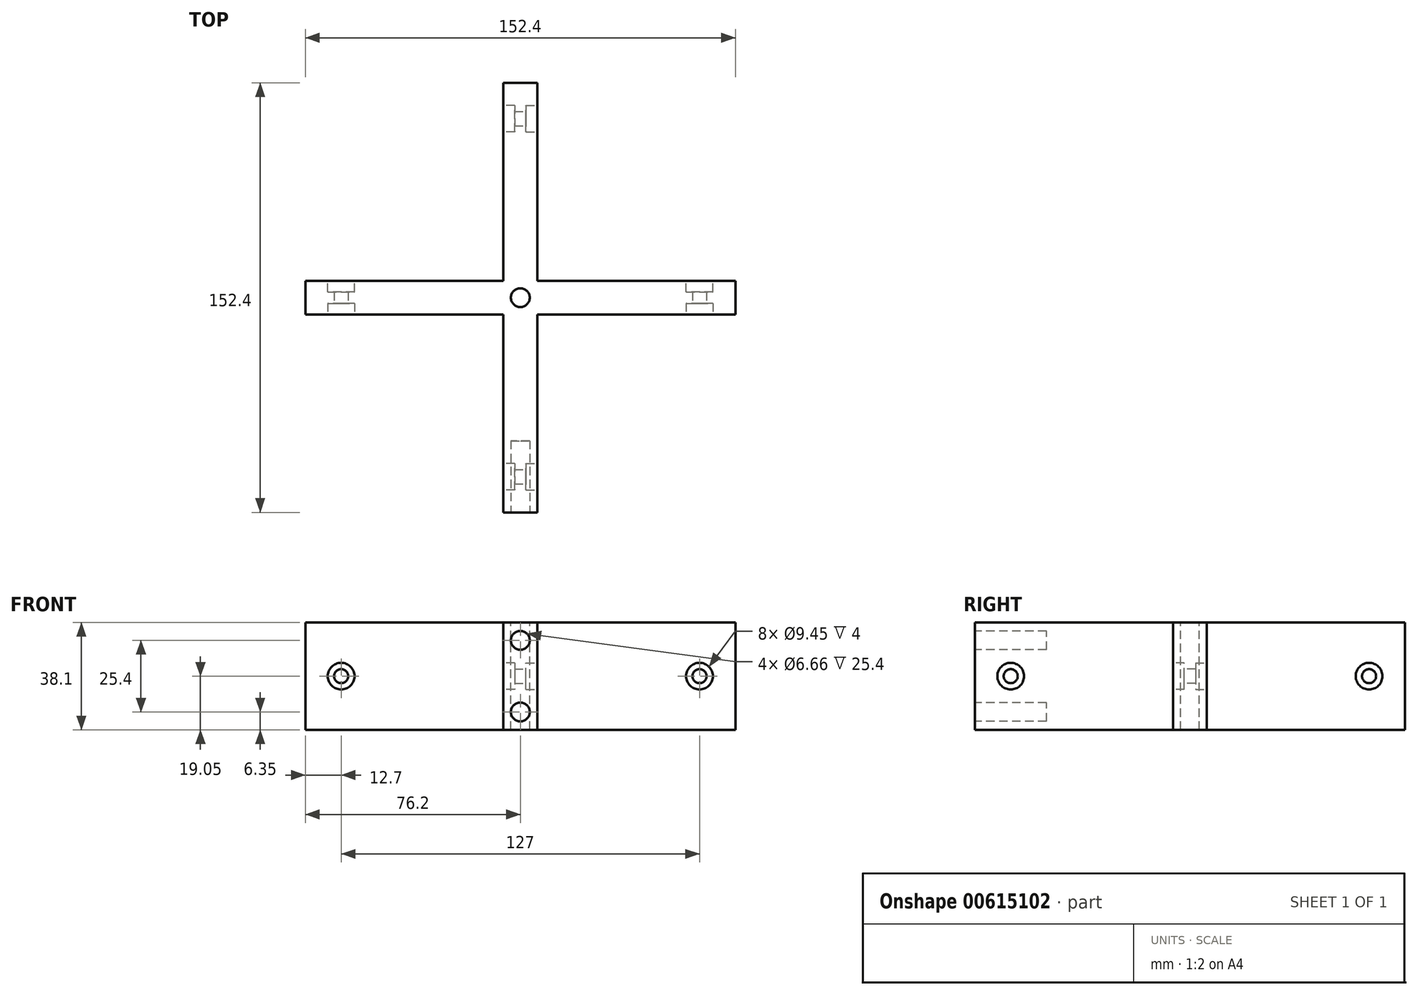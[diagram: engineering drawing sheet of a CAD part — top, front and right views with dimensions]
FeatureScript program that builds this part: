
annotation { "Feature Type Name" : "Feature", "Feature Type Description" : "" }
export const myFeature = defineFeature(function(context is Context, id is Id, definition is map)
    precondition{}
    {
        {
            var Q0;
            Q0=qCreatedBy(makeId("Top.planeOp"),FACE);
            var sketch = newSketch(context, id + "F0", { "sketchPlane" : qUnion([Q0])});
            skLineSegment(sketch, "E0.bottom", {"start": v(-6, 76.2) * mm, "end": v(6, 76.2) * mm});
            skLineSegment(sketch, "E0.top", {"start": v(-6, -76.2) * mm, "end": v(6, -76.2) * mm});
            skLineSegment(sketch, "E0.left", {"start": v(-6, 76.2) * mm, "end": v(-6, -76.2) * mm});
            skLineSegment(sketch, "E0.right", {"start": v(6, 76.2) * mm, "end": v(6, -76.2) * mm});
            skPoint(sketch, "E0.middle", {"position": v(0, 0) * mm});
            skLineSegment(sketch, "E1.bottom", {"start": v(-76.2, 6) * mm, "end": v(76.2, 6) * mm});
            skLineSegment(sketch, "E1.top", {"start": v(-76.2, -6) * mm, "end": v(76.2, -6) * mm});
            skLineSegment(sketch, "E1.left", {"start": v(-76.2, 6) * mm, "end": v(-76.2, -6) * mm});
            skLineSegment(sketch, "E1.right", {"start": v(76.2, 6) * mm, "end": v(76.2, -6) * mm});
            skSolve(sketch);
        }
        {
            var Q0;
            Q0 = qSketchRegion(id + "F0", true);
            extrude(context, id + "F1", {"entities" : qUnion([Q0]), "endBound" : BoundingType.SYMMETRIC, "depth" : 38.1 * mm, "offsetDistance" : 25.4 * mm});
        }
        {
            var Q0;
            {var subQ0=sQuery(id+"F0.wireOp",EDGE,"E0.right");Q0=makeQuery(id+"F1.opExtrude","SWEPT_FACE",FACE,{"disambiguationData":[OSD([subQ0]),TDD([makeQuery(id+"F0.imprint","IMPRINT",EDGE,{"disambiguationData":[TD([[makeQuery(id+"F0.imprint","INTERSECT",VERTEX,{"derivedFrom":[sQuery(id+"F0.wireOp",EDGE,"E0.top"),subQ0]}),1.0]])],"derivedFrom":subQ0})])]});}
            var sketch = newSketch(context, id + "F2", { "sketchPlane" : qUnion([Q0])});
            skLineSegment(sketch, "E2.0.0", {"start": v(6, -19.05) * mm, "end": v(76.2, -19.05) * mm});
            skLineSegment(sketch, "E2.0.1", {"start": v(76.2, -19.05) * mm, "end": v(76.2, 19.05) * mm});
            skLineSegment(sketch, "E2.0.2", {"start": v(76.2, 19.05) * mm, "end": v(6, 19.05) * mm});
            skLineSegment(sketch, "E2.0.3", {"start": v(6, 19.05) * mm, "end": v(6, -19.05) * mm});
            skLineSegment(sketch, "E3.0.0", {"start": v(-76.2, -19.05) * mm, "end": v(-6, -19.05) * mm});
            skLineSegment(sketch, "E3.0.1", {"start": v(-6, -19.05) * mm, "end": v(-6, 19.05) * mm});
            skLineSegment(sketch, "E3.0.2", {"start": v(-6, 19.05) * mm, "end": v(-76.2, 19.05) * mm});
            skLineSegment(sketch, "E3.0.3", {"start": v(-76.2, 19.05) * mm, "end": v(-76.2, -19.05) * mm});
            skCircle(sketch, "E4", {"center": v(-63.5, 0) * mm, "radius": 4.72 * mm});
            skCircle(sketch, "E5", {"center": v(63.5, 0) * mm, "radius": 4.72 * mm});
            skSolve(sketch);
        }
        {
            var Q0;
            Q0=makeQuery(id+"F2.imprint","IMPRINT",FACE,{"disambiguationData":[TD([[makeQuery(id+"F2.imprint","IMPRINT",EDGE,{"derivedFrom":sQuery(id+"F2.wireOp",EDGE,"E4")}),1.0]])]});
            var Q1;
            Q1=makeQuery(id+"F2.imprint","IMPRINT",FACE,{"disambiguationData":[TD([[makeQuery(id+"F2.imprint","IMPRINT",EDGE,{"derivedFrom":sQuery(id+"F2.wireOp",EDGE,"E5")}),1.0]])]});
            extrude(context, id + "F3", {"entities" : qUnion([Q0, Q1]), "operationType" : NewBodyOperationType.REMOVE, "oppositeDirection" : true, "depth" : 4 * mm, "offsetDistance" : 25.4 * mm});
        }
        {
            var Q0;
            {var subQ0=sQuery(id+"F0.wireOp",EDGE,"E0.right");Q0=makeQuery(id+"F1.opExtrude","SWEPT_FACE",FACE,{"disambiguationData":[OSD([subQ0]),TDD([makeQuery(id+"F0.imprint","IMPRINT",EDGE,{"disambiguationData":[TD([[makeQuery(id+"F0.imprint","INTERSECT",VERTEX,{"derivedFrom":[sQuery(id+"F0.wireOp",EDGE,"E0.top"),subQ0]}),1.0]])],"derivedFrom":subQ0})])]});}
            var sketch = newSketch(context, id + "F4", { "sketchPlane" : qUnion([Q0])});
            skCircle(sketch, "E6.0", {"center": v(-63.5, 0) * mm, "radius": 4.72 * mm});
            skCircle(sketch, "E7.0", {"center": v(63.5, 0) * mm, "radius": 4.72 * mm});
            skCircle(sketch, "E8", {"center": v(-63.5, 0) * mm, "radius": 2.5 * mm});
            skCircle(sketch, "E9", {"center": v(63.5, 0) * mm, "radius": 2.5 * mm});
            skSolve(sketch);
        }
        {
            var Q0;
            Q0=makeQuery(id+"F4.imprint","IMPRINT",FACE,{"disambiguationData":[TD([[makeQuery(id+"F4.imprint","IMPRINT",EDGE,{"derivedFrom":sQuery(id+"F4.wireOp",EDGE,"E8")}),1.0]])]});
            var Q1;
            Q1=makeQuery(id+"F4.imprint","IMPRINT",FACE,{"disambiguationData":[TD([[makeQuery(id+"F4.imprint","IMPRINT",EDGE,{"derivedFrom":sQuery(id+"F4.wireOp",EDGE,"E9")}),1.0]])]});
            extrude(context, id + "F5", {"entities" : qUnion([Q0, Q1]), "operationType" : NewBodyOperationType.REMOVE, "endBound" : BoundingType.THROUGH_ALL, "oppositeDirection" : true, "depth" : 6 * mm, "offsetDistance" : 25.4 * mm});
        }
        {
            var Q0;
            {var subQ0=sQuery(id+"F0.wireOp",EDGE,"E1.top");Q0=makeQuery(id+"F1.opExtrude","SWEPT_FACE",FACE,{"disambiguationData":[OSD([subQ0]),TDD([makeQuery(id+"F0.imprint","IMPRINT",EDGE,{"disambiguationData":[TD([[makeQuery(id+"F0.imprint","INTERSECT",VERTEX,{"derivedFrom":[subQ0,sQuery(id+"F0.wireOp",EDGE,"E1.left")]}),-1.0]])],"derivedFrom":subQ0})])]});}
            var sketch = newSketch(context, id + "F6", { "sketchPlane" : qUnion([Q0])});
            skLineSegment(sketch, "E10.0.0", {"start": v(-76.2, -19.05) * mm, "end": v(-6, -19.05) * mm});
            skLineSegment(sketch, "E10.0.1", {"start": v(-6, -19.05) * mm, "end": v(-6, 19.05) * mm});
            skLineSegment(sketch, "E10.0.2", {"start": v(-6, 19.05) * mm, "end": v(-76.2, 19.05) * mm});
            skLineSegment(sketch, "E10.0.3", {"start": v(-76.2, 19.05) * mm, "end": v(-76.2, -19.05) * mm});
            skLineSegment(sketch, "E11.0.0", {"start": v(6, -19.05) * mm, "end": v(76.2, -19.05) * mm});
            skLineSegment(sketch, "E11.0.1", {"start": v(76.2, -19.05) * mm, "end": v(76.2, 19.05) * mm});
            skLineSegment(sketch, "E11.0.2", {"start": v(76.2, 19.05) * mm, "end": v(6, 19.05) * mm});
            skLineSegment(sketch, "E11.0.3", {"start": v(6, 19.05) * mm, "end": v(6, -19.05) * mm});
            skCircle(sketch, "E12", {"center": v(-63.5, 0) * mm, "radius": 4.72 * mm});
            skCircle(sketch, "E13", {"center": v(63.5, 0) * mm, "radius": 4.72 * mm});
            skSolve(sketch);
        }
        {
            var Q0;
            Q0=makeQuery(id+"F6.imprint","IMPRINT",FACE,{"disambiguationData":[TD([[makeQuery(id+"F6.imprint","IMPRINT",EDGE,{"derivedFrom":sQuery(id+"F6.wireOp",EDGE,"E12")}),1.0]])]});
            var Q1;
            Q1=makeQuery(id+"F6.imprint","IMPRINT",FACE,{"disambiguationData":[TD([[makeQuery(id+"F6.imprint","IMPRINT",EDGE,{"derivedFrom":sQuery(id+"F6.wireOp",EDGE,"E13")}),1.0]])]});
            extrude(context, id + "F7", {"entities" : qUnion([Q0, Q1]), "operationType" : NewBodyOperationType.REMOVE, "oppositeDirection" : true, "depth" : 4 * mm, "offsetDistance" : 25.4 * mm});
        }
        {
            var Q0;
            {var subQ0=sQuery(id+"F0.wireOp",EDGE,"E1.top");Q0=makeQuery(id+"F1.opExtrude","SWEPT_FACE",FACE,{"disambiguationData":[OSD([subQ0]),TDD([makeQuery(id+"F0.imprint","IMPRINT",EDGE,{"disambiguationData":[TD([[makeQuery(id+"F0.imprint","INTERSECT",VERTEX,{"derivedFrom":[subQ0,sQuery(id+"F0.wireOp",EDGE,"E1.left")]}),-1.0]])],"derivedFrom":subQ0})])]});}
            var sketch = newSketch(context, id + "F8", { "sketchPlane" : qUnion([Q0])});
            skCircle(sketch, "E14.0", {"center": v(-63.5, 0) * mm, "radius": 4.72 * mm});
            skCircle(sketch, "E15.0", {"center": v(63.5, 0) * mm, "radius": 4.72 * mm});
            skCircle(sketch, "E16", {"center": v(-63.5, 0) * mm, "radius": 2.5 * mm});
            skCircle(sketch, "E17", {"center": v(63.5, 0) * mm, "radius": 2.5 * mm});
            skSolve(sketch);
        }
        {
            var Q0;
            Q0=makeQuery(id+"F8.imprint","IMPRINT",FACE,{"disambiguationData":[TD([[makeQuery(id+"F8.imprint","IMPRINT",EDGE,{"derivedFrom":sQuery(id+"F8.wireOp",EDGE,"E16")}),1.0]])]});
            var Q1;
            Q1=makeQuery(id+"F8.imprint","IMPRINT",FACE,{"disambiguationData":[TD([[makeQuery(id+"F8.imprint","IMPRINT",EDGE,{"derivedFrom":sQuery(id+"F8.wireOp",EDGE,"E17")}),1.0]])]});
            extrude(context, id + "F9", {"entities" : qUnion([Q0, Q1]), "operationType" : NewBodyOperationType.REMOVE, "endBound" : BoundingType.THROUGH_ALL, "oppositeDirection" : true, "depth" : 25.4 * mm, "offsetDistance" : 25.4 * mm});
        }
        {
            var Q0;
            {var subQ0=sQuery(id+"F0.wireOp",EDGE,"E1.bottom");Q0=makeQuery(id+"F1.opExtrude","SWEPT_FACE",FACE,{"disambiguationData":[OSD([subQ0]),TDD([makeQuery(id+"F0.imprint","IMPRINT",EDGE,{"disambiguationData":[TD([[makeQuery(id+"F0.imprint","INTERSECT",VERTEX,{"derivedFrom":[subQ0,sQuery(id+"F0.wireOp",EDGE,"E1.right")]}),1.0]])],"derivedFrom":subQ0})])]});}
            var sketch = newSketch(context, id + "F10", { "sketchPlane" : qUnion([Q0])});
            skCircle(sketch, "E18.0", {"center": v(-63.5, 0) * mm, "radius": 4.72 * mm});
            skCircle(sketch, "E19.0", {"center": v(63.5, 0) * mm, "radius": 4.72 * mm});
            skSolve(sketch);
        }
        {
            var Q0;
            Q0 = qSketchRegion(id + "F10", true);
            extrude(context, id + "F11", {"entities" : qUnion([Q0]), "operationType" : NewBodyOperationType.REMOVE, "oppositeDirection" : true, "depth" : 4 * mm, "offsetDistance" : 25.4 * mm});
        }
        {
            var Q0;
            {var subQ0=sQuery(id+"F0.wireOp",EDGE,"E0.left");Q0=makeQuery(id+"F1.opExtrude","SWEPT_FACE",FACE,{"disambiguationData":[OSD([subQ0]),TDD([makeQuery(id+"F0.imprint","IMPRINT",EDGE,{"disambiguationData":[TD([[makeQuery(id+"F0.imprint","INTERSECT",VERTEX,{"derivedFrom":[sQuery(id+"F0.wireOp",EDGE,"E0.bottom"),subQ0]}),-1.0]])],"derivedFrom":subQ0})])]});}
            var sketch = newSketch(context, id + "F12", { "sketchPlane" : qUnion([Q0])});
            skCircle(sketch, "E20.0", {"center": v(-63.5, 0) * mm, "radius": 4.72 * mm});
            skCircle(sketch, "E21.0", {"center": v(63.5, 0) * mm, "radius": 4.72 * mm});
            skSolve(sketch);
        }
        {
            var Q0;
            Q0 = qSketchRegion(id + "F12", true);
            extrude(context, id + "F13", {"entities" : qUnion([Q0]), "operationType" : NewBodyOperationType.REMOVE, "oppositeDirection" : true, "depth" : 4 * mm, "offsetDistance" : 25.4 * mm});
        }
        {
            var Q0;
            Q0=makeQuery(id+"F1.opExtrude","CAP_FACE",FACE,{"disambiguationData":[OSD([sQuery(id+"F0.wireOp",EDGE,"E0.bottom"),sQuery(id+"F0.wireOp",EDGE,"E0.top"),sQuery(id+"F0.wireOp",EDGE,"E0.left"),sQuery(id+"F0.wireOp",EDGE,"E0.right"),sQuery(id+"F0.wireOp",EDGE,"E1.bottom"),sQuery(id+"F0.wireOp",EDGE,"E1.top"),sQuery(id+"F0.wireOp",EDGE,"E1.left"),sQuery(id+"F0.wireOp",EDGE,"E1.right")])],"isStart":false});
            var sketch = newSketch(context, id + "F14", { "sketchPlane" : qUnion([Q0])});
            skCircle(sketch, "E22", {"center": v(0, 0) * mm, "radius": 3.33 * mm});
            skSolve(sketch);
        }
        {
            var Q0;
            Q0 = qSketchRegion(id + "F14", true);
            extrude(context, id + "F15", {"entities" : qUnion([Q0]), "operationType" : NewBodyOperationType.REMOVE, "endBound" : BoundingType.THROUGH_ALL, "oppositeDirection" : true, "depth" : 25.4 * mm, "offsetDistance" : 25.4 * mm});
        }
        {
            var Q0;
            Q0=makeQuery(id+"F1.opExtrude","SWEPT_FACE",FACE,{"disambiguationData":[OSD([sQuery(id+"F0.wireOp",EDGE,"E0.top")])]});
            var sketch = newSketch(context, id + "F16", { "sketchPlane" : qUnion([Q0])});
            skCircle(sketch, "E23", {"center": v(0, 12.7) * mm, "radius": 3.33 * mm});
            skCircle(sketch, "E24", {"center": v(0, -12.7) * mm, "radius": 3.33 * mm});
            skSolve(sketch);
        }
        {
            var Q0;
            Q0 = qSketchRegion(id + "F16", true);
            extrude(context, id + "F17", {"entities" : qUnion([Q0]), "operationType" : NewBodyOperationType.REMOVE, "oppositeDirection" : true, "depth" : 25.4 * mm, "offsetDistance" : 25.4 * mm});
        }
    });
